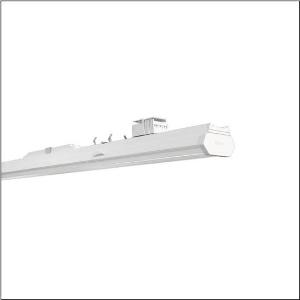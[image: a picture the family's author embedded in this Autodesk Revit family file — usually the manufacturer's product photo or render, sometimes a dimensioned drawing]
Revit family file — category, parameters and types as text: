
# Revit family: licross_r__21_protected_ho_52tp12dn4dxm_cc4f
name_source: partatom
category: Lighting Fixtures
units: mm (PartAtom-declared; Revit-internal decimal feet)

## family parameters
Cut with Voids When Loaded = No
Host = Face
Light Source = No
Part Type = Normal
Room Calculation Point = No
Round Connector Dimension = Use Diameter
Shared = No

## types (1)
- --- (1 x LED, 13000 lm, 74.3 W, 4000K)
    Apparent Load = 74 VA
    CIE Flux Codes = 70 91 97 98 100
    Color Rendering = 80
    Color Temperature = 4000K
    Default Elevation = 1800 mm
    Description = Licross® 21 Protected HO, luminaire insert, of sheet steel, galvanised, coil coated, white, length: 1.500mm, width: 90mm, height: 103mm, LED rated luminous flux: 13.000lm, light colour: 840, control gear: DALI 2, with plug, 5-pole, with phase selection, mains connection: 220..240V, AC, 50/60Hz, rated input power: 74W, halogen-free wiring, primary light control with lens, of plastic, primary optical cover: cover, of PMMA, light emission: direct distribution, primary light characteristic: symmetric, protection rating (complete): IP64, insulation class (complete): insulation class I (protective earthing), certification: CE, ENEC, VDE, UKCA, protection symbol: D if used in an environment with conductive dust loads with corresponding accessories, impact resistance: IK06, permissible ambient temperature for indoor applications: -25..+40°C, corresponds to IFS (International Featured Standards) requirements for safety and quality in the food industry, reducing of maximum allowable ambient temperature of 5°C with ceiling mounting, LABS conformity tested according to VDMA 24364:2018-05, packaging unit: 1 piece
    Height = 92 mm
    Lamp = 1 x LED
    Lamp Light Flux = 13000 lm
    Lamp Power = 74.3 W
    Lamp count = 1
    Length = 1500 mm
    Luminous efficacy = 175 lm/W
    Manufacturer = Siteco
    ModVariant = No
    Model = 52TP12DN4DXM
    Mounting Place = Ceiling
    Mounting Type = Pendant
    Number of Poles = 1
    OnlyDefault = Yes
    Power Factor = 1
    Product Name = Licross® 21 Protected HO
    Product group = luminaire insert
    ProductGroupID = 901
    Protection Class = Protection class I
    Protection Degree = IP 64
    RLX_Detail_Level = 1
    RLX_Emergency_Light_Flux = 0 lm
    RLX_Emergency_Type = 0
    RLX_Emergency_Type_DB = No
    RlxData = <blob elided: 24445 chars, md5=80e4d19e>
    Socket = socket
    Standby Power = 0 W
    System Light Flux = 13000 lm
    System Power = 74 W
    Type Comments = factory setting: luminous flux: 100 % | dim-lin: 254 | 424 mA
    Type Image = l_1256148.jpg
    URL = http://relux.com
    VarID = @adj_099147
    Voltage = 0 V
    Weight = 0.00 kg
    Width = 88 mm

## geometry (parser evidence)
native form markers: Blend x4, Sweep x9
no freeform markers — native parametric forms only
